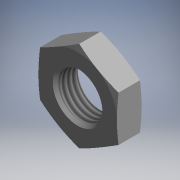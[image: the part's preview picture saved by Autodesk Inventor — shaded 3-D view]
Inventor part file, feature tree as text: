
AUTODESK INVENTOR PART (.ipt)
format: ipt  version: 2017.3 (Build 213256000, 256)  size: 126,976 bytes
history: native  units: mm (DEFAULTED — no unit token found)
features: other x14, sketch x3, revolve x2, extrude x1, thread x1
ambient origin geometry x8: Origin, YZ Plane, XZ Plane, XY Plane, X Axis, Y Axis, Z Axis, Center Point
bodies: Solid1 (feature_tree)
feature tree (21):
  revolve  "Revolution1"  [1 undecoded]
  extrude  "Extrusion1"  Depth=4.647mm TaperAngle=0.0deg
  revolve  "Revolution2"  [1 undecoded]
  thread  "Thread1"  [1 undecoded]
  other  "2CYL_XY"
  other  "2CYL_YZ"
  other  "2CYL_ZX"
  other  "2CYL_X"
  other  "2CYL_Y"
  other  "2CYL_Z"
  other  "2CYL_Center"
  other  "din439b_punkt_XY"
  other  "din439b_punkt_YZ"
  other  "din439b_punkt_ZX"
  other  "din439b_punkt_X"
  other  "din439b_punkt_Y"
  other  "din439b_punkt_Z"
  other  "din439b_punkt_Center"
  sketch  "Sketch_1"  dims[d0=360.0deg d1=14.0mm d2=0.0mm]
  sketch  "Sketch_2"  dims[d3=360.0deg d4=4.647mm d5=0.0mm]
  sketch  "Sketch_3"  dims[d6=0.0mm]
note: 3 required parameter values undecoded (feature->parameter linkage not recoverable at this tier; creation-order binding heuristic only, values carry confidence <= 0.55)